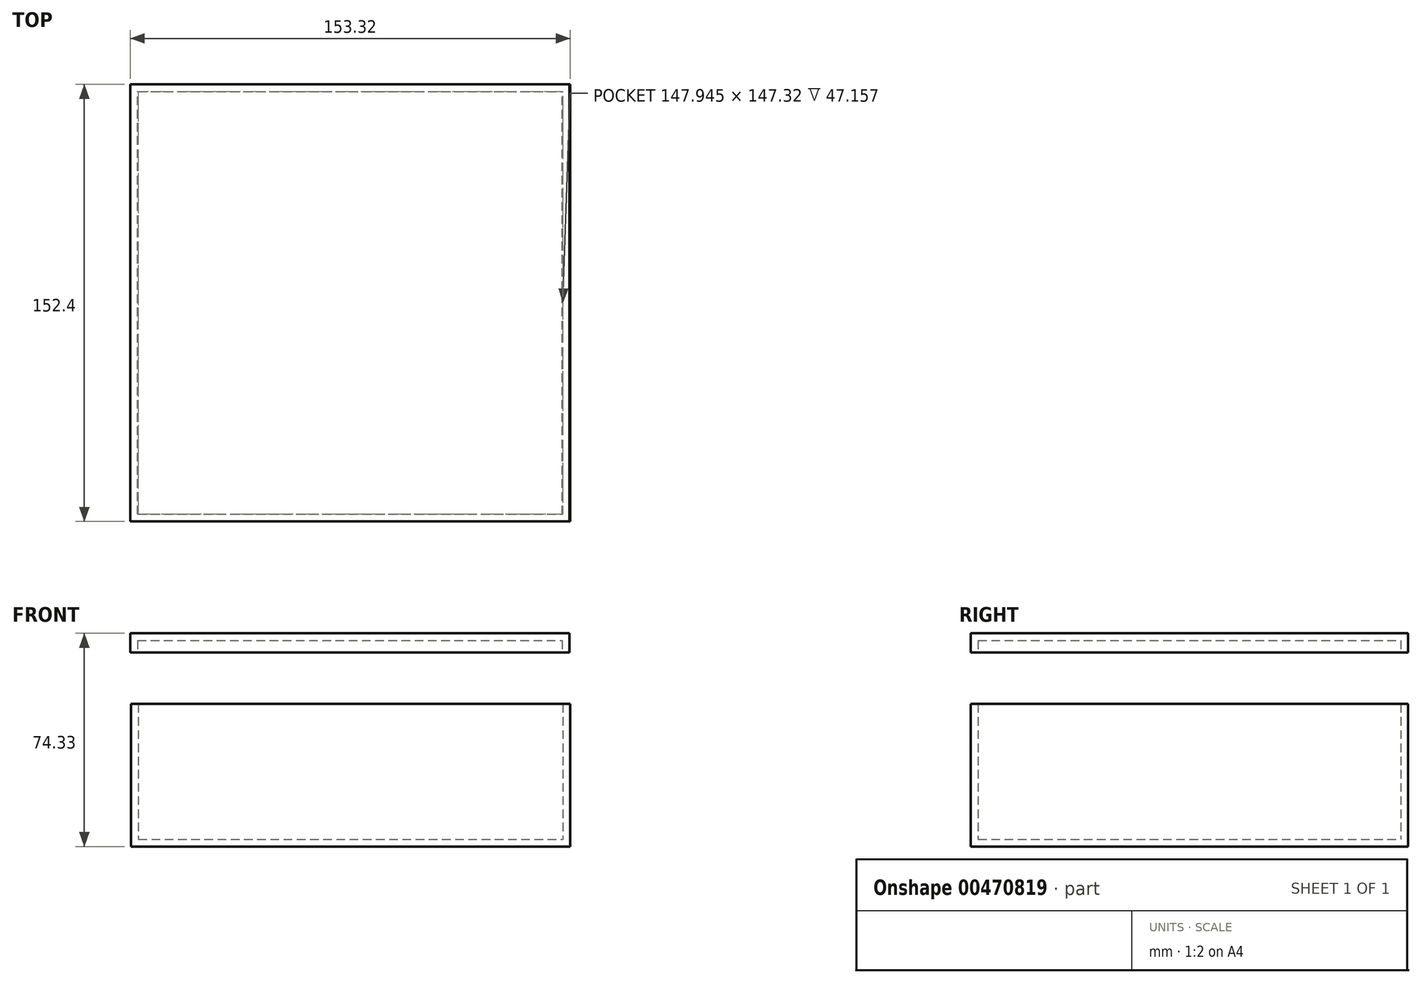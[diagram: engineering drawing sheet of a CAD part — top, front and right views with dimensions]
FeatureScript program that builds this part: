
annotation { "Feature Type Name" : "Feature", "Feature Type Description" : "" }
export const myFeature = defineFeature(function(context is Context, id is Id, definition is map)
    precondition{}
    {
        {
            var Q0;
            Q0=qCreatedBy(makeId("Front.planeOp"),FACE);
            var sketch = newSketch(context, id + "F0", { "sketchPlane" : qUnion([Q0])});
            skLineSegment(sketch, "E0.bottom", {"start": v(-76.37, 0) * mm, "end": v(76.66, 0) * mm});
            skLineSegment(sketch, "E0.top", {"start": v(-76.37, -49.7) * mm, "end": v(76.66, -49.7) * mm});
            skLineSegment(sketch, "E0.left", {"start": v(-76.37, 0) * mm, "end": v(-76.37, -49.7) * mm});
            skLineSegment(sketch, "E0.right", {"start": v(76.66, 0) * mm, "end": v(76.66, -49.7) * mm});
            skLineSegment(sketch, "E1.bottom", {"start": v(-76.66, 24.63) * mm, "end": v(76.37, 24.63) * mm});
            skLineSegment(sketch, "E1.top", {"start": v(-76.66, 17.93) * mm, "end": v(76.37, 17.93) * mm});
            skLineSegment(sketch, "E1.left", {"start": v(-76.66, 24.63) * mm, "end": v(-76.66, 17.93) * mm});
            skLineSegment(sketch, "E1.right", {"start": v(76.37, 24.63) * mm, "end": v(76.37, 17.93) * mm});
            skSolve(sketch);
        }
        {
            var Q0;
            Q0=makeQuery(id+"F0.imprint","IMPRINT",FACE,{"disambiguationData":[TD([[makeQuery(id+"F0.imprint","IMPRINT",EDGE,{"derivedFrom":sQuery(id+"F0.wireOp",EDGE,"E1.bottom")}),-1.0]])]});
            var Q1;
            Q1=makeQuery(id+"F0.imprint","IMPRINT",FACE,{"disambiguationData":[TD([[makeQuery(id+"F0.imprint","IMPRINT",EDGE,{"derivedFrom":sQuery(id+"F0.wireOp",EDGE,"E0.bottom")}),-1.0]])]});
            extrude(context, id + "F1", {"entities" : qUnion([Q0, Q1]), "depth" : 152.4 * mm});
        }
        {
            var Q0;
            Q0=makeQuery(id+"F1.opExtrude","SWEPT_FACE",FACE,{"disambiguationData":[OSD([sQuery(id+"F0.wireOp",EDGE,"E1.top")])]});
            shell(context, id + "F2", {"entities" : qUnion([Q0]), "thickness" : 2.54 * mm});
        }
        {
            var Q0;
            Q0=makeQuery(id+"F1.opExtrude","SWEPT_FACE",FACE,{"disambiguationData":[OSD([sQuery(id+"F0.wireOp",EDGE,"E0.bottom")])]});
            shell(context, id + "F3", {"entities" : qUnion([Q0]), "thickness" : 2.54 * mm});
        }
    });
